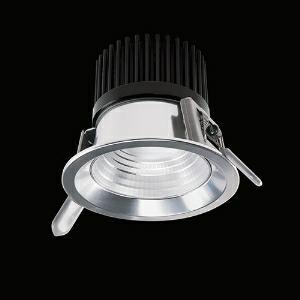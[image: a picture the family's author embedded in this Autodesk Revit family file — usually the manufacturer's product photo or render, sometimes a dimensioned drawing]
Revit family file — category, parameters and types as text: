
# Revit family: spectral_myral_myral_3500-830-f-dali
name_source: partatom
category: Lighting Fixtures
revit_build: Autodesk Revit 2016 (Build: 20150220_1215(x64)
units: mm (PartAtom-declared; Revit-internal decimal feet)

## family parameters
Cut with Voids When Loaded = No
Host = Face
Light Source = No
Part Type = Normal
Room Calculation Point = No
Round Connector Dimension = Use Diameter
Shared = No

## types (1)
- SPECTRAL MYRAL (1 x )
    Apparent Load = 0 VA
    Approval mark = CE
    CIE Flux Codes = 81 99 100 100 100
    Control Gear = Electronic transformer
    Default Elevation = 1800 mm
    Description = SPG0330186
MYRAL recessed spot

Design:
    Height = 0 mm  [stored 0 ft]
    Lamp = 1 x
    Lamp count = 1
    Length = 120 mm
    Luminous efficacy = 0 lm/W
    Manufacturer = Ridi
    ModVariant = No
    Model = MYRAL 3500-830-F-DALI
    Mounting Place = Ceiling
    Mounting Type = Recessed
    Number of Poles = 1
    OnlyDefault = Yes
    Power Factor = 1
    Product Name = SPECTRAL MYRAL
    Product group = Downlight recessed
    ProductGroupID = 400
    Protection Class = Protection class
    Protection Degree = IP 20
    RlxData = <blob elided: 38905 chars, md5=75aaabf5>
    Socket = socket
    Standby Power = 0 W
    System Light Flux = 0 lm
    System Power = 0 W
    Type Image = myral_04.jpg
    URL = http://reluxnet.relux.com
    VarID = ---
    Voltage = 0 V
    Weight = 0.00 kg
    Width = 0 mm  [stored 0 ft]

note: [stored X ft] marks values corroborated as IEEE doubles in the binary element streams (Revit-internal decimal feet)

## geometry (parser evidence)
native form markers: Sweep x9
no freeform markers — native parametric forms only
